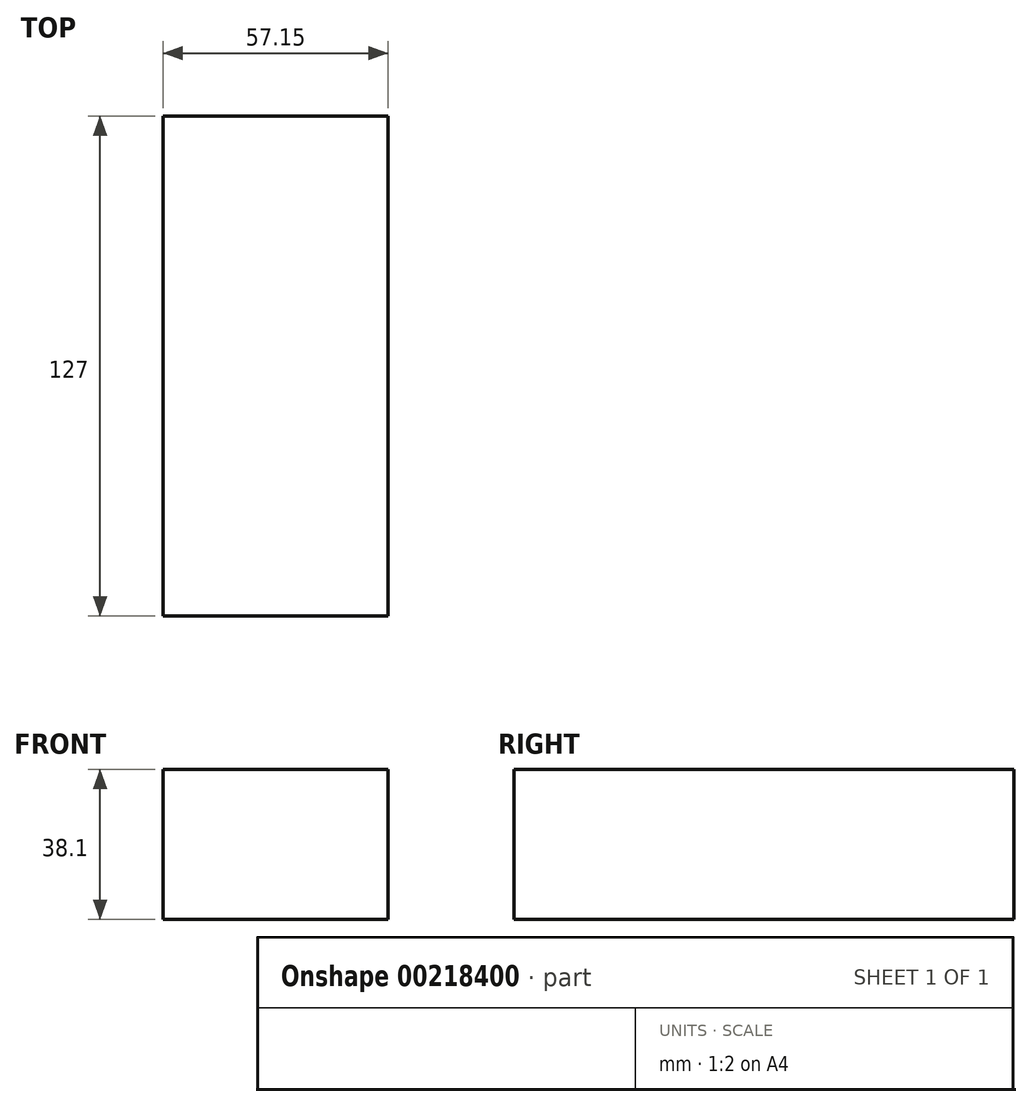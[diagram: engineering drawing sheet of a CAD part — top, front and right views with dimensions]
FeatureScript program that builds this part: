
annotation { "Feature Type Name" : "Feature", "Feature Type Description" : "" }
export const myFeature = defineFeature(function(context is Context, id is Id, definition is map)
    precondition{}
    {
        {
            var Q0;
            Q0=qCreatedBy(makeId("Front.planeOp"),FACE);
            var sketch = newSketch(context, id + "F0", { "sketchPlane" : qUnion([Q0])});
            skLineSegment(sketch, "E0.bottom", {"start": v(3.8, -16) * mm, "end": v(-53.34, -16) * mm});
            skLineSegment(sketch, "E0.top", {"start": v(3.8, 22.1) * mm, "end": v(-53.34, 22.1) * mm});
            skLineSegment(sketch, "E0.left", {"start": v(3.8, -16) * mm, "end": v(3.8, 22.1) * mm});
            skLineSegment(sketch, "E0.right", {"start": v(-53.34, -16) * mm, "end": v(-53.34, 22.1) * mm});
            skPoint(sketch, "E0.middle", {"position": v(-24.77, 3.05) * mm});
            skSolve(sketch);
        }
        {
            var Q0;
            Q0=makeQuery(id+"F0.imprint","IMPRINT",FACE,{"disambiguationData":[TD([[makeQuery(id+"F0.imprint","IMPRINT",EDGE,{"derivedFrom":sQuery(id+"F0.wireOp",EDGE,"E0.bottom")}),-1.0]])]});
            extrude(context, id + "F1", {"entities" : qUnion([Q0]), "endBound" : BoundingType.SYMMETRIC, "depth" : 127 * mm});
        }
    });
